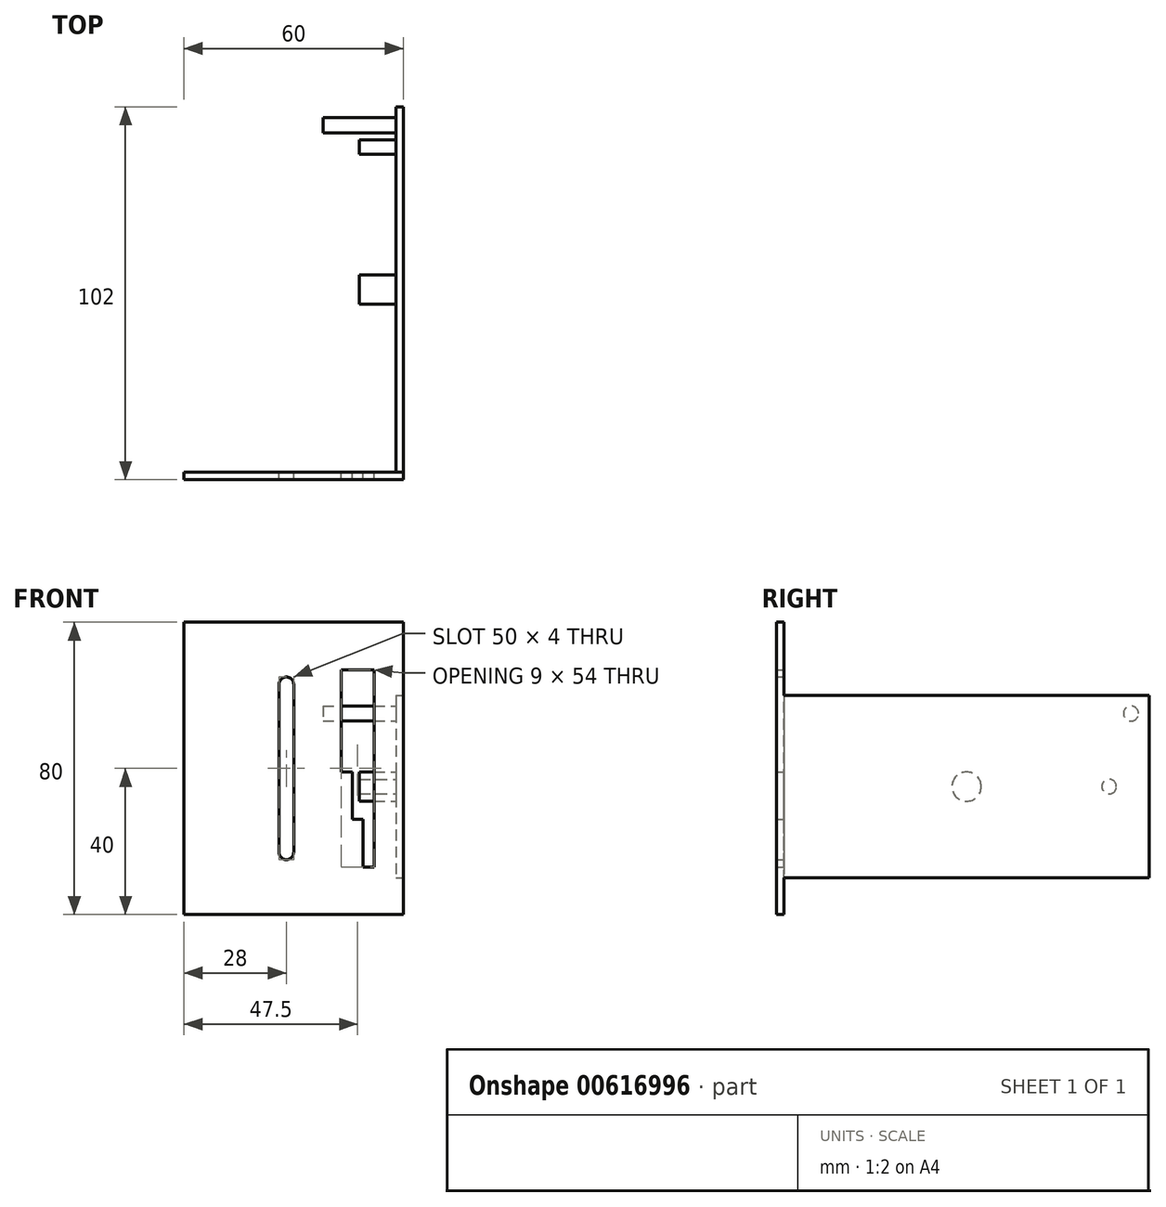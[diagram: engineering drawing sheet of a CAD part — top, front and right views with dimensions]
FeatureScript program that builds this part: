
annotation { "Feature Type Name" : "Feature", "Feature Type Description" : "" }
export const myFeature = defineFeature(function(context is Context, id is Id, definition is map)
    precondition{}
    {
        {
            var Q0;
            Q0=qCreatedBy(makeId("Front.planeOp"),FACE);
            var sketch = newSketch(context, id + "F0", { "sketchPlane" : qUnion([Q0])});
            skLineSegment(sketch, "E0.bottom", {"start": v(0, 0) * mm, "end": v(60, 0) * mm});
            skLineSegment(sketch, "E0.top", {"start": v(0, 80) * mm, "end": v(60, 80) * mm});
            skLineSegment(sketch, "E0.left", {"start": v(0, 0) * mm, "end": v(0, 80) * mm});
            skLineSegment(sketch, "E0.right", {"start": v(60, 0) * mm, "end": v(60, 80) * mm});
            skLineSegment(sketch, "E1", {"start": v(52, 67) * mm, "end": v(52, 13) * mm});
            skLineSegment(sketch, "E2", {"start": v(52, 13) * mm, "end": v(49, 13) * mm});
            skLineSegment(sketch, "E3", {"start": v(49, 13) * mm, "end": v(49, 26) * mm});
            skLineSegment(sketch, "E4", {"start": v(49, 26) * mm, "end": v(46, 26) * mm});
            skLineSegment(sketch, "E5", {"start": v(46, 26) * mm, "end": v(46, 39) * mm});
            skLineSegment(sketch, "E6", {"start": v(46, 39) * mm, "end": v(43, 39) * mm});
            skLineSegment(sketch, "E7", {"start": v(52, 67) * mm, "end": v(43, 67) * mm});
            skLineSegment(sketch, "E8", {"start": v(43, 67) * mm, "end": v(43, 39) * mm});
            skLineSegment(sketch, "E9", {"start": v(26, 63) * mm, "end": v(26, 17) * mm});
            skArc(sketch, "E10", {"start": v(30, 63) * mm, "mid": v(28, 65) * mm, "end": v(26, 63) * mm});
            skLineSegment(sketch, "E11", {"start": v(30, 63) * mm, "end": v(30, 17) * mm});
            skArc(sketch, "E12", {"start": v(26, 17) * mm, "mid": v(28, 15) * mm, "end": v(30, 17) * mm});
            skLineSegment(sketch, "E13", {"start": v(58, 60) * mm, "end": v(60, 60) * mm});
            skLineSegment(sketch, "E14", {"start": v(58, 60) * mm, "end": v(58, 10) * mm});
            skLineSegment(sketch, "E15", {"start": v(58, 10) * mm, "end": v(60, 10) * mm});
            skSolve(sketch);
        }
        {
            var Q0;
            Q0=makeQuery(id+"F0.imprint","IMPRINT",FACE,{"disambiguationData":[TD([[makeQuery(id+"F0.imprint","IMPRINT",EDGE,{"derivedFrom":sQuery(id+"F0.wireOp",EDGE,"E0.bottom")}),1.0]])]});
            var Q1;
            {var subQ0=sQuery(id+"F0.wireOp",EDGE,"E0.left");Q1=makeQuery(id+"F0.imprint","IMPRINT",FACE,{"disambiguationData":[TD([[makeQuery(id+"F0.imprint","IMPRINT",EDGE,{"derivedFrom":subQ0}),-1.0]])]});}
            var Q2;
            {var subQ0=sQuery(id+"F0.wireOp",EDGE,"E13");Q2=makeQuery(id+"F0.imprint","IMPRINT",FACE,{"disambiguationData":[TD([[makeQuery(id+"F0.imprint","IMPRINT",EDGE,{"derivedFrom":subQ0}),-1.0]])]});}
            extrude(context, id + "F1", {"entities" : qUnion([Q0, Q1, Q2]), "depth" : 2 * mm, "offsetDistance" : 25 * mm});
        }
        {
            var Q0;
            {var subQ0=sQuery(id+"F0.wireOp",EDGE,"E13");Q0=makeQuery(id+"F0.imprint","IMPRINT",FACE,{"disambiguationData":[TD([[makeQuery(id+"F0.imprint","IMPRINT",EDGE,{"derivedFrom":subQ0}),-1.0]])]});}
            extrude(context, id + "F2", {"entities" : qUnion([Q0]), "operationType" : NewBodyOperationType.ADD, "oppositeDirection" : true, "depth" : 100 * mm, "offsetDistance" : 25 * mm});
        }
        {
            var Q0;
            Q0=makeQuery(id+"F2.opExtrude","SWEPT_FACE",FACE,{"disambiguationData":[OSD([sQuery(id+"F0.wireOp",EDGE,"E14")])]});
            var sketch = newSketch(context, id + "F3", { "sketchPlane" : qUnion([Q0])});
            skCircle(sketch, "E16", {"center": v(-50, 35) * mm, "radius": 4 * mm});
            skPoint(sketch, "E16.centerSnap0", {"position": v(-100, 35) * mm});
            skPoint(sketch, "E16.centerSnap1", {"position": v(-50, 60) * mm});
            skCircle(sketch, "E17", {"center": v(-95, 55) * mm, "radius": 2.06 * mm});
            skCircle(sketch, "E18", {"center": v(-89, 35) * mm, "radius": 2 * mm});
            skSolve(sketch);
        }
        {
            var Q0;
            Q0=makeQuery(id+"F3.imprint","IMPRINT",FACE,{"disambiguationData":[TD([[makeQuery(id+"F3.imprint","IMPRINT",EDGE,{"derivedFrom":sQuery(id+"F3.wireOp",EDGE,"E16")}),1.0]])]});
            var Q1;
            Q1=makeQuery(id+"F3.imprint","IMPRINT",FACE,{"disambiguationData":[TD([[makeQuery(id+"F3.imprint","IMPRINT",EDGE,{"derivedFrom":sQuery(id+"F3.wireOp",EDGE,"E18")}),1.0]])]});
            extrude(context, id + "F4", {"entities" : qUnion([Q0, Q1]), "operationType" : NewBodyOperationType.ADD, "depth" : 10 * mm, "offsetDistance" : 25 * mm});
        }
        {
            var Q0;
            Q0=makeQuery(id+"F3.imprint","IMPRINT",FACE,{"disambiguationData":[TD([[makeQuery(id+"F3.imprint","IMPRINT",EDGE,{"derivedFrom":sQuery(id+"F3.wireOp",EDGE,"E17")}),1.0]])]});
            extrude(context, id + "F5", {"entities" : qUnion([Q0]), "operationType" : NewBodyOperationType.ADD, "depth" : 20 * mm, "offsetDistance" : 25 * mm});
        }
    });
